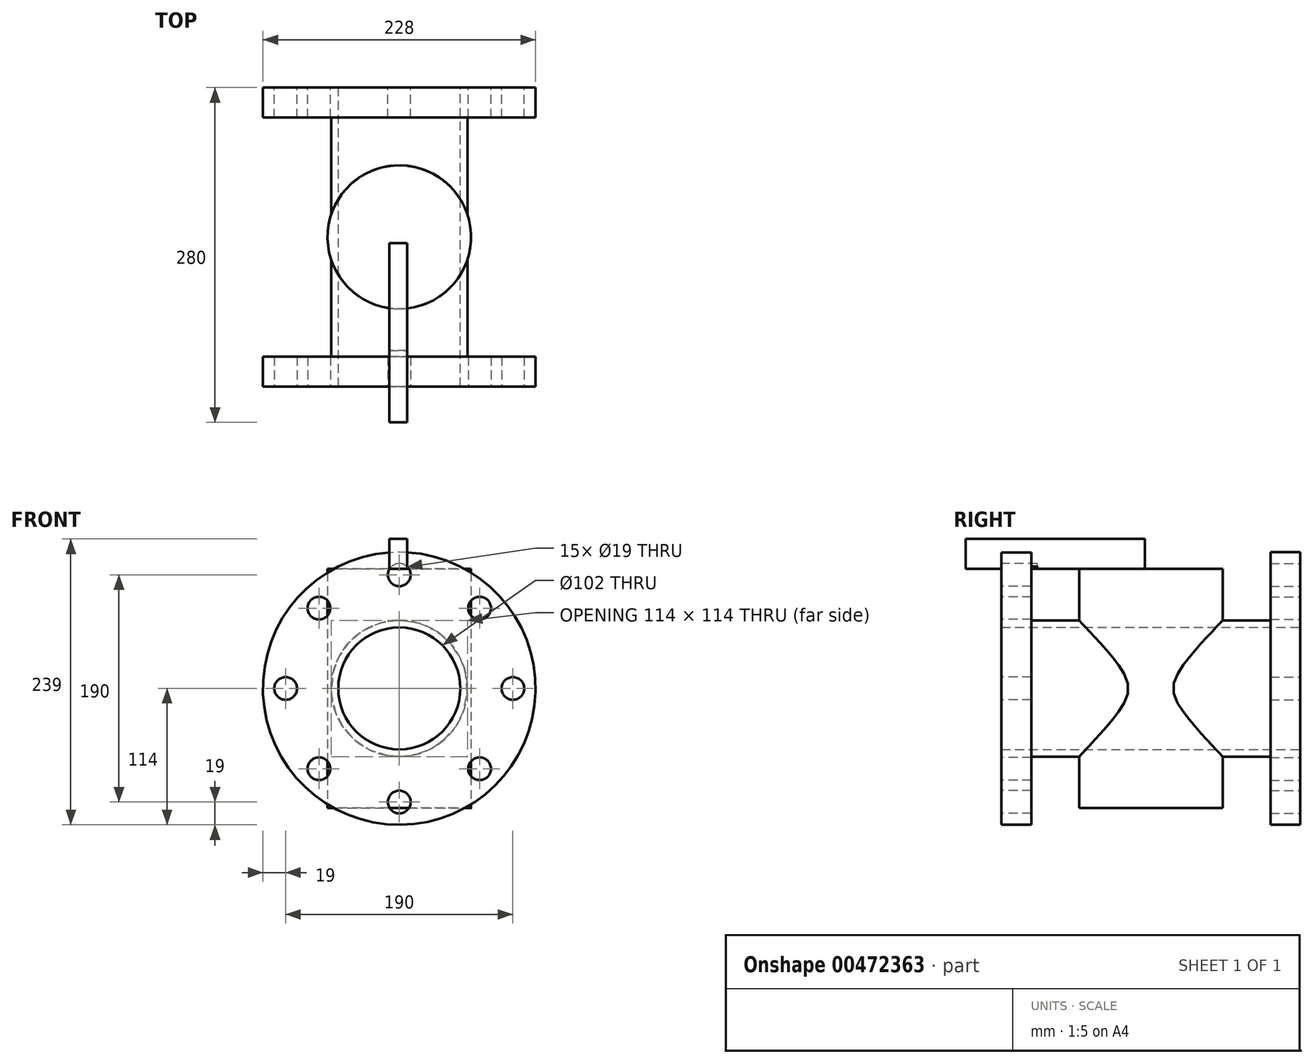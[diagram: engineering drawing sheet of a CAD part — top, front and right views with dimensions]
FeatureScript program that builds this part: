
annotation { "Feature Type Name" : "Feature", "Feature Type Description" : "" }
export const myFeature = defineFeature(function(context is Context, id is Id, definition is map)
    precondition{}
    {
        {
            var Q0;
            Q0=qCreatedBy(makeId("Front.planeOp"),FACE);
            var sketch = newSketch(context, id + "F0", { "sketchPlane" : qUnion([Q0])});
            skCircle(sketch, "E0", {"center": v(0, 0) * mm, "radius": 114 * mm});
            skSolve(sketch);
        }
        {
            var Q0;
            Q0 = qSketchRegion(id + "F0", true);
            extrude(context, id + "F1", {"entities" : qUnion([Q0]), "depth" : 25 * mm});
        }
        {
            var Q0;
            Q0=makeQuery(id+"F1.opExtrude","CAP_FACE",FACE,{"disambiguationData":[OSD([sQuery(id+"F0.wireOp",EDGE,"E0")])],"isStart":false});
            var sketch = newSketch(context, id + "F2", { "sketchPlane" : qUnion([Q0])});
            skCircle(sketch, "E1", {"center": v(0, 0) * mm, "radius": 57 * mm});
            skSolve(sketch);
        }
        {
            var Q0;
            Q0 = qSketchRegion(id + "F2", true);
            extrude(context, id + "F3", {"entities" : qUnion([Q0]), "operationType" : NewBodyOperationType.ADD, "depth" : 200 * mm});
        }
        {
            var Q0;
            Q0=makeQuery(id+"F3.opExtrude","CAP_FACE",FACE,{"disambiguationData":[OSD([sQuery(id+"F2.wireOp",EDGE,"E1")])],"isStart":false});
            var sketch = newSketch(context, id + "F4", { "sketchPlane" : qUnion([Q0])});
            skCircle(sketch, "E2", {"center": v(0, 0) * mm, "radius": 114 * mm});
            skSolve(sketch);
        }
        {
            var Q0;
            Q0 = qSketchRegion(id + "F4", true);
            extrude(context, id + "F5", {"entities" : qUnion([Q0]), "operationType" : NewBodyOperationType.ADD, "depth" : 25 * mm});
        }
        {
            var Q0;
            Q0=qCreatedBy(makeId("Top.planeOp"),FACE);
            var sketch = newSketch(context, id + "F6", { "sketchPlane" : qUnion([Q0])});
            skCircle(sketch, "E3", {"center": v(0, -125) * mm, "radius": 60 * mm});
            skSolve(sketch);
        }
        {
            var Q0;
            Q0 = qSketchRegion(id + "F6", true);
            extrude(context, id + "F7", {"entities" : qUnion([Q0]), "operationType" : NewBodyOperationType.ADD, "endBound" : BoundingType.SYMMETRIC, "depth" : 200 * mm});
        }
        {
            var Q0;
            Q0=makeQuery(id+"F7.opExtrude","CAP_FACE",FACE,{"disambiguationData":[OSD([sQuery(id+"F6.wireOp",EDGE,"E3")])],"isStart":false});
            var sketch = newSketch(context, id + "F8", { "sketchPlane" : qUnion([Q0])});
            skLineSegment(sketch, "E4.bottom", {"start": v(-8.38, -130) * mm, "end": v(6.62, -130) * mm});
            skLineSegment(sketch, "E4.top", {"start": v(-8.38, -280) * mm, "end": v(6.62, -280) * mm});
            skLineSegment(sketch, "E4.left", {"start": v(-8.38, -130) * mm, "end": v(-8.38, -280) * mm});
            skLineSegment(sketch, "E4.right", {"start": v(6.62, -130) * mm, "end": v(6.62, -280) * mm});
            skSolve(sketch);
        }
        {
            var Q0;
            Q0 = qSketchRegion(id + "F8", true);
            extrude(context, id + "F9", {"entities" : qUnion([Q0]), "operationType" : NewBodyOperationType.ADD, "depth" : 25 * mm});
        }
        {
            var Q0;
            Q0=makeQuery(id+"F5.opExtrude","CAP_FACE",FACE,{"disambiguationData":[OSD([sQuery(id+"F4.wireOp",EDGE,"E2")])],"isStart":false});
            var sketch = newSketch(context, id + "F10", { "sketchPlane" : qUnion([Q0])});
            skCircle(sketch, "E5", {"center": v(0, 95) * mm, "radius": 9.5 * mm});
            skCircle(sketch, "E6.1.0", {"center": v(-67.18, 67.18) * mm, "radius": 9.5 * mm});
            skCircle(sketch, "E6.2.0", {"center": v(-95, 0) * mm, "radius": 9.5 * mm});
            skCircle(sketch, "E6.3.0", {"center": v(-67.18, -67.18) * mm, "radius": 9.5 * mm});
            skCircle(sketch, "E6.4.0", {"center": v(0, -95) * mm, "radius": 9.5 * mm});
            skCircle(sketch, "E6.5.0", {"center": v(67.18, -67.18) * mm, "radius": 9.5 * mm});
            skCircle(sketch, "E6.6.0", {"center": v(95, 0) * mm, "radius": 9.5 * mm});
            skPoint(sketch, "E6.center", {"position": v(0, 0) * mm});
            skCircle(sketch, "E7.1.7.0", {"center": v(67.18, 67.18) * mm, "radius": 9.5 * mm});
            skSolve(sketch);
        }
        {
            var Q0;
            Q0 = qSketchRegion(id + "F10", true);
            extrude(context, id + "F11", {"entities" : qUnion([Q0]), "operationType" : NewBodyOperationType.REMOVE, "oppositeDirection" : true, "depth" : 30 * mm});
        }
        {
            var Q0;
            Q0=makeQuery(id+"F1.opExtrude","CAP_FACE",FACE,{"disambiguationData":[OSD([sQuery(id+"F0.wireOp",EDGE,"E0")])],"isStart":true});
            var sketch = newSketch(context, id + "F12", { "sketchPlane" : qUnion([Q0])});
            skCircle(sketch, "E8", {"center": v(0, 95) * mm, "radius": 9.5 * mm});
            skCircle(sketch, "E9.1.0", {"center": v(-67.18, 67.18) * mm, "radius": 9.5 * mm});
            skCircle(sketch, "E9.2.0", {"center": v(-95, 0) * mm, "radius": 9.5 * mm});
            skCircle(sketch, "E9.3.0", {"center": v(-67.18, -67.18) * mm, "radius": 9.5 * mm});
            skCircle(sketch, "E9.4.0", {"center": v(0, -95) * mm, "radius": 9.5 * mm});
            skCircle(sketch, "E9.5.0", {"center": v(67.18, -67.18) * mm, "radius": 9.5 * mm});
            skCircle(sketch, "E9.6.0", {"center": v(95, 0) * mm, "radius": 9.5 * mm});
            skCircle(sketch, "E9.7.0", {"center": v(67.18, 67.18) * mm, "radius": 9.5 * mm});
            skPoint(sketch, "E9.center", {"position": v(0, 0) * mm});
            skSolve(sketch);
        }
        {
            var Q0;
            Q0 = qSketchRegion(id + "F12", true);
            extrude(context, id + "F13", {"entities" : qUnion([Q0]), "operationType" : NewBodyOperationType.REMOVE, "oppositeDirection" : true, "depth" : 30 * mm});
        }
        {
            var Q0;
            Q0=makeQuery(id+"F1.opExtrude","CAP_FACE",FACE,{"disambiguationData":[OSD([sQuery(id+"F0.wireOp",EDGE,"E0")])],"isStart":true});
            var sketch = newSketch(context, id + "F14", { "sketchPlane" : qUnion([Q0])});
            skCircle(sketch, "E10", {"center": v(0, 0) * mm, "radius": 51 * mm});
            skSolve(sketch);
        }
        {
            var Q0;
            Q0 = qSketchRegion(id + "F14", true);
            extrude(context, id + "F15", {"entities" : qUnion([Q0]), "operationType" : NewBodyOperationType.REMOVE, "oppositeDirection" : true, "depth" : 1000 * mm});
        }
    });
